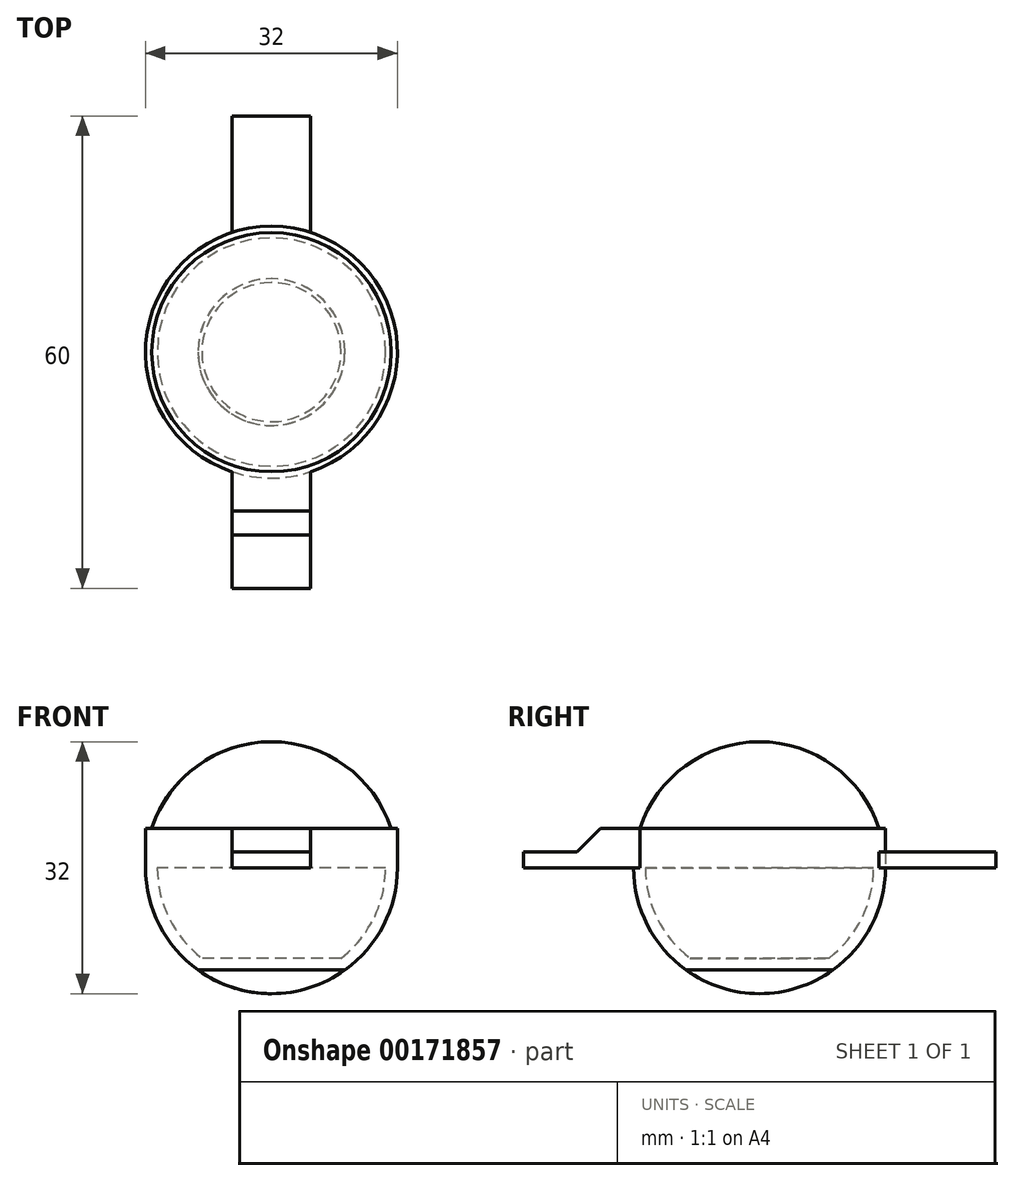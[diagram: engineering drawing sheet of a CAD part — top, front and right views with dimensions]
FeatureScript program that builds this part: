
annotation { "Feature Type Name" : "Feature", "Feature Type Description" : "" }
export const myFeature = defineFeature(function(context is Context, id is Id, definition is map)
    precondition{}
    {
        {
            var Q0;
            Q0=qCreatedBy(makeId("Front.planeOp"),FACE);
            var sketch = newSketch(context, id + "F0", { "sketchPlane" : qUnion([Q0])});
            skArc(sketch, "E0", {"start": v(0, -16) * mm, "mid": v(16, 0) * mm, "end": v(0, 16) * mm});
            skLineSegment(sketch, "E1", {"start": v(0, 16) * mm, "end": v(0, -16) * mm});
            skSolve(sketch);
        }
        {
            var Q0;
            Q0=makeQuery(id+"F0.imprint","IMPRINT",FACE,{"disambiguationData":[TD([[makeQuery(id+"F0.imprint","IMPRINT",EDGE,{"derivedFrom":sQuery(id+"F0.wireOp",EDGE,"E0")}),1.0]])]});
            var Q1;
            Q1=sQuery(id+"F0.wireOp",EDGE,"E1");
            revolve(context, id + "F1", {"entities" : qUnion([Q0]), "axis" : qUnion([Q1]), "revolveType" : RevolveType.FULL});
        }
        {
            var Q0;
            Q0=qCreatedBy(makeId("Top.planeOp"),FACE);
            var sketch = newSketch(context, id + "F2", { "sketchPlane" : qUnion([Q0])});
            skCircle(sketch, "E2", {"center": v(0, 0) * mm, "radius": 46.2 * mm});
            skSolve(sketch);
        }
        {
            var Q0;
            Q0 = qSketchRegion(id + "F2", true);
            extrude(context, id + "F3", {"entities" : qUnion([Q0]), "operationType" : NewBodyOperationType.REMOVE, "depth" : 25 * mm});
        }
        {
            var Q0;
            Q0=qCreatedBy(makeId("Top.planeOp"),FACE);
            cPlane(context, id + "F4", {"entities" : qUnion([Q0]), "cplaneType" : CPlaneType.OFFSET, "offset" : 16 * mm, "oppositeDirection" : true, "width" : 150 * mm, "height" : 150 * mm});
        }
        {
            var Q0;
            Q0=qCreatedBy(id+"F4.planeOp",FACE);
            var sketch = newSketch(context, id + "F5", { "sketchPlane" : qUnion([Q0])});
            skCircle(sketch, "E3", {"center": v(0, 0) * mm, "radius": 29 * mm});
            skSolve(sketch);
        }
        {
            var Q0;
            Q0 = qSketchRegion(id + "F5", true);
            extrude(context, id + "F6", {"entities" : qUnion([Q0]), "operationType" : NewBodyOperationType.REMOVE, "depth" : 3 * mm});
        }
        {
            var Q0;
            Q0 = qSketchRegion(id + "F0", true);
            var Q1;
            Q1=sQuery(id+"F0.wireOp",EDGE,"E1");
            revolve(context, id + "F7", {"entities" : qUnion([Q0]), "axis" : qUnion([Q1]), "revolveType" : RevolveType.FULL});
        }
        {
            var Q0;
            Q0=makeQuery(id+"F1.opRevolve","SWEPT_BODY",BODY,{"disambiguationData":[OSD([sQuery(id+"F0.wireOp",EDGE,"E0"),sQuery(id+"F0.wireOp",EDGE,"E1")])]});
            var Q1;
            Q1=makeQuery(id+"F7.opRevolve","SWEPT_BODY",BODY,{"disambiguationData":[OSD([sQuery(id+"F0.wireOp",EDGE,"E0"),sQuery(id+"F0.wireOp",EDGE,"E1")])]});
            booleanBodies(context, id + "F8", {"operationType" : BooleanOperationType.SUBTRACTION, "tools" : qUnion([Q0]), "targets" : qUnion([Q1]), "keepTools" : true});
        }
        {
            var Q0;
            Q0=makeQuery(id+"F3.boolean.opBoolean","COPY",FACE,{"derivedFrom":makeQuery(id+"F3.opExtrude","CAP_FACE",FACE,{"disambiguationData":[OSD([sQuery(id+"F2.wireOp",EDGE,"E2")])],"isStart":true})});
            shell(context, id + "F9", {"entities" : qUnion([Q0]), "thickness" : 1.5 * mm});
        }
        {
            var Q0;
            Q0=makeQuery(id+"F3.boolean.opBoolean","COPY",FACE,{"derivedFrom":makeQuery(id+"F3.opExtrude","CAP_FACE",FACE,{"disambiguationData":[OSD([sQuery(id+"F2.wireOp",EDGE,"E2")])],"isStart":true})});
            var sketch = newSketch(context, id + "F10", { "sketchPlane" : qUnion([Q0])});
            skCircle(sketch, "E4.0", {"center": v(0, 0) * mm, "radius": 16 * mm});
            skCircle(sketch, "E5.0", {"center": v(0, 0) * mm, "radius": 14.5 * mm});
            skSolve(sketch);
        }
        {
            var Q0;
            Q0 = qSketchRegion(id + "F10", true);
            extrude(context, id + "F11", {"entities" : qUnion([Q0]), "operationType" : NewBodyOperationType.ADD, "depth" : 5 * mm});
        }
        {
            var Q0;
            Q0=qCreatedBy(makeId("Top.planeOp"),FACE);
            var sketch = newSketch(context, id + "F12", { "sketchPlane" : qUnion([Q0])});
            skCircle(sketch, "E6.0", {"center": v(0, 0) * mm, "radius": 16 * mm});
            skLineSegment(sketch, "E7.bottom", {"start": v(5, 30) * mm, "end": v(-5, 30) * mm});
            skLineSegment(sketch, "E7.top", {"start": v(5, -30) * mm, "end": v(-5, -30) * mm});
            skLineSegment(sketch, "E7.left", {"start": v(5, 30) * mm, "end": v(5, -30) * mm});
            skLineSegment(sketch, "E7.right", {"start": v(-5, 30) * mm, "end": v(-5, -30) * mm});
            skSolve(sketch);
        }
        {
            var Q0;
            {var subQ5=sQuery(id+"F12.wireOp",EDGE,"E7.top");Q0=makeQuery(id+"F12.imprint","IMPRINT",FACE,{"disambiguationData":[TD([[makeQuery(id+"F12.imprint","IMPRINT",EDGE,{"derivedFrom":subQ5}),-1.0]])]});}
            var Q1;
            {var subQ5=sQuery(id+"F12.wireOp",EDGE,"E7.bottom");Q1=makeQuery(id+"F12.imprint","IMPRINT",FACE,{"disambiguationData":[TD([[makeQuery(id+"F12.imprint","IMPRINT",EDGE,{"derivedFrom":subQ5}),1.0]])]});}
            extrude(context, id + "F13", {"entities" : qUnion([Q0, Q1]), "depth" : 2 * mm});
        }
        {
            var Q0;
            Q0=makeQuery(id+"F11.opExtrude","CAP_FACE",FACE,{"disambiguationData":[OSD([sQuery(id+"F10.wireOp",EDGE,"E4.0"),sQuery(id+"F10.wireOp",EDGE,"E5.0")])],"isStart":false});
            var sketch = newSketch(context, id + "F14", { "sketchPlane" : qUnion([Q0])});
            skCircle(sketch, "E8.0", {"center": v(0, 0) * mm, "radius": 16 * mm});
            skLineSegment(sketch, "E9.bottom", {"start": v(-5, -15.2) * mm, "end": v(5, -15.2) * mm});
            skLineSegment(sketch, "E9.top", {"start": v(-5, -20.2) * mm, "end": v(5, -20.2) * mm});
            skLineSegment(sketch, "E9.left", {"start": v(-5, -15.2) * mm, "end": v(-5, -20.2) * mm});
            skLineSegment(sketch, "E9.right", {"start": v(5, -15.2) * mm, "end": v(5, -20.2) * mm});
            skSolve(sketch);
        }
        {
            var Q0;
            Q0=makeQuery(id+"F14.imprint","IMPRINT",FACE,{"disambiguationData":[TD([[makeQuery(id+"F14.imprint","IMPRINT",EDGE,{"derivedFrom":sQuery(id+"F14.wireOp",EDGE,"E9.top")}),1.0]])]});
            var Q1;
            Q1=makeQuery(id+"F13.opExtrude","CAP_FACE",FACE,{"disambiguationData":[OSD([sQuery(id+"F12.wireOp",EDGE,"E6.0"),sQuery(id+"F12.wireOp",EDGE,"E7.top"),sQuery(id+"F12.wireOp",EDGE,"E7.left"),sQuery(id+"F12.wireOp",EDGE,"E7.right")])],"isStart":false});
            extrude(context, id + "F15", {"entities" : qUnion([Q0]), "operationType" : NewBodyOperationType.ADD, "endBound" : BoundingType.UP_TO_SURFACE, "oppositeDirection" : true, "endBoundEntityFace" : qUnion([Q1]), "depth" : 25 * mm});
        }
        {
            var Q0;
            Q0=makeQuery(id+"F15.opExtrude","CAP_EDGE",EDGE,{"disambiguationData":[OSD([sQuery(id+"F14.wireOp",EDGE,"E9.top")])],"isStart":false});
            chamfer(context, id + "F16", {"entities" : qUnion([Q0]), "width" : 3 * mm, "tangentPropagation" : true});
        }
    });
